# Revit family: Midea_VRF_HydroModule_SMK_140
name_source: partatom
category: Mechanical Equipment
revit_build: Autodesk Revit 2013 (Build: 20120221_2030(x64)
units: mm (PartAtom-declared; Revit-internal decimal feet)

## types (1)
- SMK-140/RN3
    Casing color = SB2014
    Compressor = 1
    Condensation = water
    Depth = 450.000 mm
    Description = High efficiency water cooled
    Gas = R134a
    Gas pipe = 15.900 mm
    Heating Capacity = 14.000 kW
    Height = 795.000 mm
    Installation = Indoor installation
    MCA (Minimum Circuit Amps) = 16 A
    Manufacturer = Midea
    Maximum Fuse Amps = 20 A
    Model = SMK-140/RN3
    Net Weight = 58.00 kg
    Power supply = 220-240V 1N~50Hz/60Hz
    Refrigerant pipe gas side = 12.700 mm
    Refrigerant pipe liquid side = 9.520 mm
    Series = Hydro Module
    Water pipes diameter (external groove) = 25.400 mm
    Width = 300.000 mm
    clearance access front = 600.000 mm
    clearance access left = 100.000 mm
    clearance access right = 400.000 mm

## geometry (parser evidence)
native form markers: Sweep x7
no freeform markers — native parametric forms only
